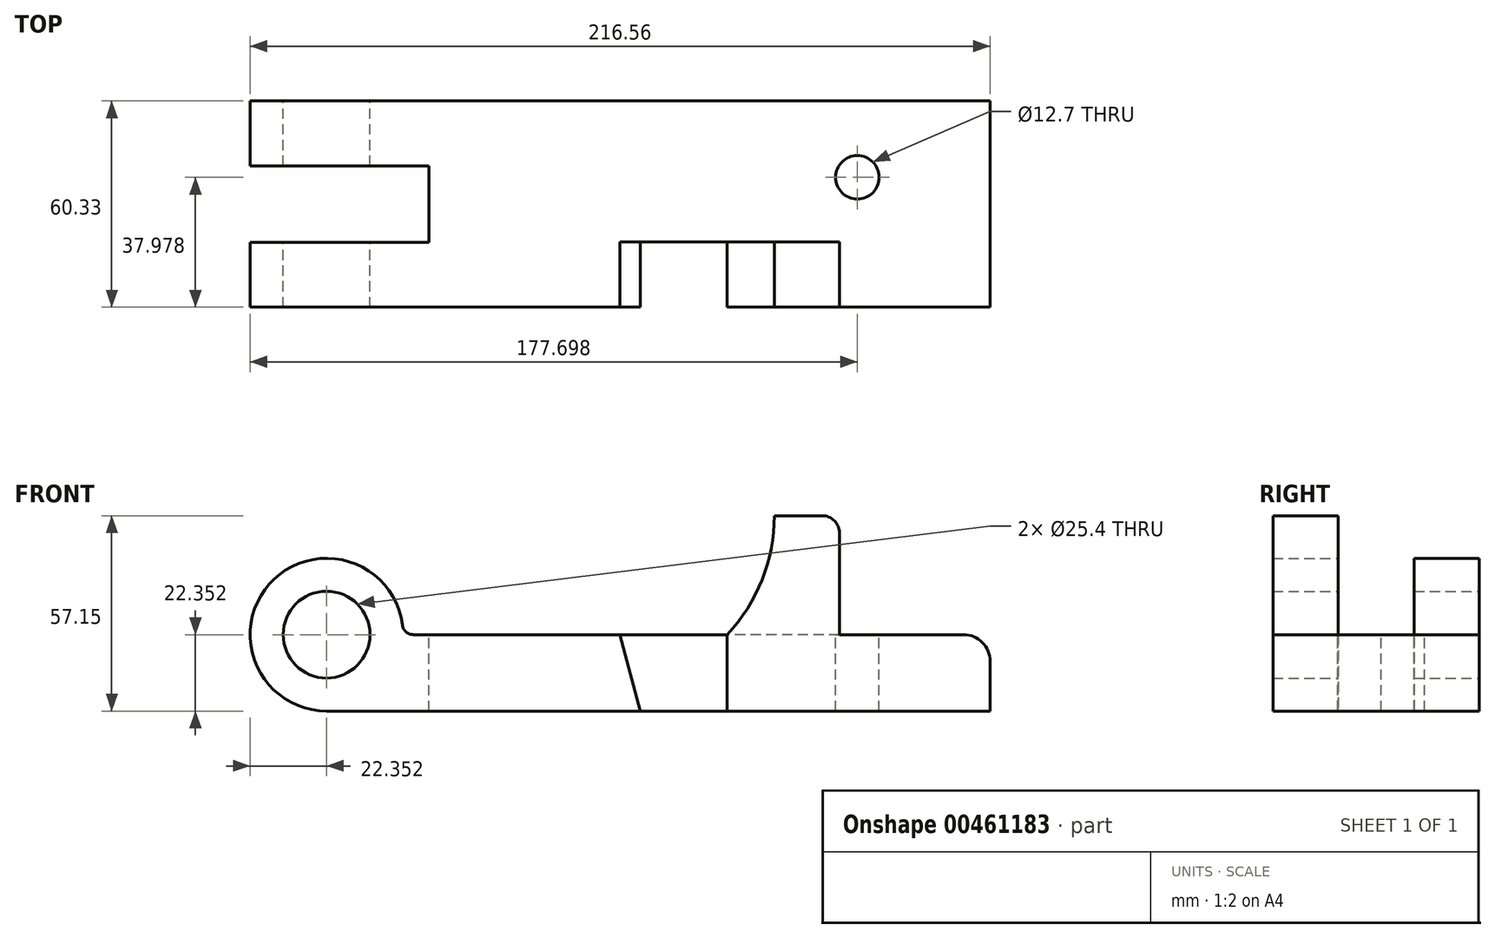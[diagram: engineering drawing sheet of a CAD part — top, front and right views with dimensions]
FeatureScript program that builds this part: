
annotation { "Feature Type Name" : "Feature", "Feature Type Description" : "" }
export const myFeature = defineFeature(function(context is Context, id is Id, definition is map)
    precondition{}
    {
        {
            var Q0;
            Q0=qCreatedBy(makeId("Front.planeOp"),FACE);
            var sketch = newSketch(context, id + "F0", { "sketchPlane" : qUnion([Q0])});
            skLineSegment(sketch, "E0", {"start": v(0, 0) * mm, "end": v(0, 14.48) * mm});
            skLineSegment(sketch, "E1", {"start": v(-7.87, 22.35) * mm, "end": v(-44.12, 22.35) * mm});
            skLineSegment(sketch, "E2", {"start": v(-44.12, 22.35) * mm, "end": v(-44.12, 52.07) * mm});
            skLineSegment(sketch, "E3", {"start": v(-49.2, 57.15) * mm, "end": v(-76.96, 57.15) * mm});
            skLineSegment(sketch, "E4", {"start": v(-76.96, 57.15) * mm, "end": v(-76.96, 22.35) * mm});
            skLineSegment(sketch, "E5", {"start": v(-76.96, 22.35) * mm, "end": v(-171.86, 22.35) * mm});
            skLineSegment(sketch, "E6", {"start": v(-194.2, 0) * mm, "end": v(0, 0) * mm});
            skArc(sketch, "E7", {"start": v(-171.86, 22.35) * mm, "mid": v(-210.01, 38.16) * mm, "end": v(-194.2, 0) * mm});
            skCircle(sketch, "E8", {"center": v(-194.2, 22.35) * mm, "radius": 12.7 * mm});
            skCircle(sketch, "E9", {"center": v(-113.97, 57.15) * mm, "radius": 50.8 * mm});
            skLineSegment(sketch, "E10", {"start": v(-76.96, 22.35) * mm, "end": v(-76.96, 0) * mm});
            skLineSegment(sketch, "E11", {"start": v(-108.36, 22.35) * mm, "end": v(-102.36, 0) * mm});
            skPoint(sketch, "E12.visualSharp", {"position": v(-44.12, 57.15) * mm});
            skArc(sketch, "E12.filletArc", {"start": v(-44.12, 52.07) * mm, "mid": v(-45.6, 55.66) * mm, "end": v(-49.2, 57.15) * mm});
            skPoint(sketch, "E13.visualSharp", {"position": v(0, 22.35) * mm});
            skArc(sketch, "E13.filletArc", {"start": v(0, 14.48) * mm, "mid": v(-2.3, 20.05) * mm, "end": v(-7.87, 22.35) * mm});
            skLineSegment(sketch, "E14", {"start": v(-44.12, 22.35) * mm, "end": v(-76.96, 22.35) * mm});
            skLineSegment(sketch, "E15", {"start": v(-194.2, 22.35) * mm, "end": v(-194.2, 9.65) * mm, "construction": true});
            skLineSegment(sketch, "E16.trimOffspring", {"start": v(-194.2, 59.62) * mm, "end": v(-194.2, 0) * mm, "construction": true});
            skSolve(sketch);
        }
        {
            var Q0;
            {var subQ0=sQuery(id+"F0.wireOp",EDGE,"E7");Q0=makeQuery(id+"F0.imprint","IMPRINT",FACE,{"disambiguationData":[TD([[makeQuery(id+"F0.imprint","IMPRINT",EDGE,{"derivedFrom":subQ0}),1.0]])]});}
            var Q1;
            {var subQ0=sQuery(id+"F0.wireOp",EDGE,"E11");var subQ1=sQuery(id+"F0.wireOp",EDGE,"E5");var subQ2=makeQuery(id+"F0.imprint","INTERSECT",VERTEX,{"derivedFrom":[subQ1,subQ0]});Q1=makeQuery(id+"F0.imprint","IMPRINT",FACE,{"disambiguationData":[TD([[makeQuery(id+"F0.imprint","IMPRINT",EDGE,{"disambiguationData":[TD([[subQ2,-1.0]])],"derivedFrom":subQ1}),1.0]])]});}
            var Q2;
            {var subQ1=sQuery(id+"F0.wireOp",EDGE,"E5");var subQ3=sQuery(id+"F0.wireOp",EDGE,"E11");var subQ4=makeQuery(id+"F0.imprint","INTERSECT",VERTEX,{"derivedFrom":[subQ1,subQ3]});Q2=makeQuery(id+"F0.imprint","IMPRINT",FACE,{"disambiguationData":[TD([[makeQuery(id+"F0.imprint","IMPRINT",EDGE,{"disambiguationData":[TD([[subQ4,-1.0]])],"derivedFrom":subQ3}),1.0]])]});}
            var Q3;
            {var subQ0=sQuery(id+"F0.wireOp",EDGE,"E10");Q3=makeQuery(id+"F0.imprint","IMPRINT",FACE,{"disambiguationData":[TD([[makeQuery(id+"F0.imprint","IMPRINT",EDGE,{"derivedFrom":subQ0}),-1.0]])]});}
            var Q4;
            {var subQ2=sQuery(id+"F0.wireOp",EDGE,"E0");Q4=makeQuery(id+"F0.imprint","IMPRINT",FACE,{"disambiguationData":[TD([[makeQuery(id+"F0.imprint","IMPRINT",EDGE,{"derivedFrom":subQ2}),1.0]])]});}
            extrude(context, id + "F1", {"entities" : qUnion([Q0, Q1, Q2, Q3, Q4]), "depth" : 60.32 * mm});
        }
        {
            var Q0;
            Q0=makeQuery(id+"F1.opExtrude","CAP_FACE",FACE,{"disambiguationData":[OSD([sQuery(id+"F0.wireOp",EDGE,"E0"),sQuery(id+"F0.wireOp",EDGE,"E1"),sQuery(id+"F0.wireOp",EDGE,"E5"),sQuery(id+"F0.wireOp",EDGE,"E6"),sQuery(id+"F0.wireOp",EDGE,"E7"),sQuery(id+"F0.wireOp",EDGE,"E8"),sQuery(id+"F0.wireOp",EDGE,"E13.filletArc"),sQuery(id+"F0.wireOp",EDGE,"E14")])],"isStart":false});
            var sketch = newSketch(context, id + "F2", { "sketchPlane" : qUnion([Q0])});
            skLineSegment(sketch, "E17.0", {"start": v(-76.96, 22.35) * mm, "end": v(-76.96, 0) * mm});
            skLineSegment(sketch, "E18.0", {"start": v(-108.36, 22.35) * mm, "end": v(-102.36, 0) * mm});
            skLineSegment(sketch, "E19.0", {"start": v(-49.2, 57.15) * mm, "end": v(-76.96, 57.15) * mm});
            skCircle(sketch, "E20.0", {"center": v(-113.97, 57.15) * mm, "radius": 50.8 * mm});
            skLineSegment(sketch, "E21.0", {"start": v(-76.96, 57.15) * mm, "end": v(-76.96, 22.35) * mm});
            skLineSegment(sketch, "E22.0", {"start": v(-76.96, 22.35) * mm, "end": v(-171.86, 22.35) * mm});
            skLineSegment(sketch, "E23.0", {"start": v(-194.2, 0) * mm, "end": v(0, 0) * mm});
            skLineSegment(sketch, "E24.0", {"start": v(-44.12, 22.35) * mm, "end": v(-44.12, 52.07) * mm});
            skArc(sketch, "E25.0", {"start": v(-44.12, 52.07) * mm, "mid": v(-45.6, 55.66) * mm, "end": v(-49.2, 57.15) * mm});
            skLineSegment(sketch, "E26.0", {"start": v(-44.12, 22.35) * mm, "end": v(-76.96, 22.35) * mm});
            skSolve(sketch);
        }
        {
            var Q0;
            Q0=makeQuery(id+"F2.imprint","IMPRINT",FACE,{"disambiguationData":[TD([[makeQuery(id+"F2.imprint","IMPRINT",EDGE,{"derivedFrom":sQuery(id+"F2.wireOp",EDGE,"E24.0")}),1.0]])]});
            extrude(context, id + "F3", {"entities" : qUnion([Q0]), "operationType" : NewBodyOperationType.ADD, "oppositeDirection" : true, "depth" : 19.05 * mm});
        }
        {
            var Q0;
            {var subQ0=sQuery(id+"F2.wireOp",EDGE,"E22.0");var subQ1=sQuery(id+"F2.wireOp",EDGE,"E18.0");var subQ2=makeQuery(id+"F2.imprint","INTERSECT",VERTEX,{"derivedFrom":[subQ1,subQ0]});Q0=makeQuery(id+"F2.imprint","IMPRINT",FACE,{"disambiguationData":[TD([[makeQuery(id+"F2.imprint","IMPRINT",EDGE,{"disambiguationData":[TD([[subQ2,-1.0]])],"derivedFrom":subQ1}),1.0]])]});}
            var Q1;
            {var subQ0=sQuery(id+"F2.wireOp",EDGE,"E17.0");Q1=makeQuery(id+"F2.imprint","IMPRINT",FACE,{"disambiguationData":[TD([[makeQuery(id+"F2.imprint","IMPRINT",EDGE,{"derivedFrom":subQ0}),-1.0]])]});}
            extrude(context, id + "F4", {"entities" : qUnion([Q0, Q1]), "operationType" : NewBodyOperationType.REMOVE, "oppositeDirection" : true, "depth" : 19.05 * mm});
        }
        {
            var Q0;
            Q0=makeQuery(id+"F1.opExtrude","SWEPT_FACE",FACE,{"disambiguationData":[OSD([sQuery(id+"F0.wireOp",EDGE,"E1"),sQuery(id+"F0.wireOp",EDGE,"E5"),sQuery(id+"F0.wireOp",EDGE,"E14")])]});
            var sketch = newSketch(context, id + "F5", { "sketchPlane" : qUnion([Q0])});
            skCircle(sketch, "E27", {"center": v(-38.86, -22.35) * mm, "radius": 6.35 * mm});
            skSolve(sketch);
        }
        {
            var Q0;
            Q0 = qSketchRegion(id + "F5", true);
            var Q1;
            Q1=makeQuery(id+"F1.opExtrude","SWEPT_FACE",FACE,{"disambiguationData":[OSD([sQuery(id+"F0.wireOp",EDGE,"E6")])]});
            extrude(context, id + "F6", {"entities" : qUnion([Q0]), "operationType" : NewBodyOperationType.REMOVE, "endBound" : BoundingType.UP_TO_SURFACE, "oppositeDirection" : true, "endBoundEntityFace" : qUnion([Q1]), "depth" : 25.4 * mm});
        }
        {
            var Q0;
            Q0=makeQuery(id+"F1.opExtrude","SWEPT_FACE",FACE,{"disambiguationData":[OSD([sQuery(id+"F0.wireOp",EDGE,"E1"),sQuery(id+"F0.wireOp",EDGE,"E5"),sQuery(id+"F0.wireOp",EDGE,"E14")])]});
            var sketch = newSketch(context, id + "F7", { "sketchPlane" : qUnion([Q0])});
            skLineSegment(sketch, "E28.bottom", {"start": v(-233.73, -19) * mm, "end": v(-164.24, -19) * mm});
            skLineSegment(sketch, "E28.top", {"start": v(-233.73, -41.33) * mm, "end": v(-164.24, -41.33) * mm});
            skLineSegment(sketch, "E28.left", {"start": v(-233.73, -19) * mm, "end": v(-233.73, -41.33) * mm});
            skLineSegment(sketch, "E28.right", {"start": v(-164.24, -19) * mm, "end": v(-164.24, -41.33) * mm});
            skSolve(sketch);
        }
        {
            var Q0;
            Q0=makeQuery(id+"F1.opExtrude","SWEPT_EDGE",EDGE,{"disambiguationData":[OSD([sQuery(id+"F0.wireOp",EDGE,"E5"),sQuery(id+"F0.wireOp",EDGE,"E7")])]});
            var Q1;
            Q1=makeQuery(id+"F3.opExtrude","SWEPT_EDGE",EDGE,{"disambiguationData":[OSD([sQuery(id+"F0.wireOp",EDGE,"E1"),sQuery(id+"F0.wireOp",EDGE,"E5"),sQuery(id+"F0.wireOp",EDGE,"E14"),sQuery(id+"F2.wireOp",EDGE,"E24.0"),sQuery(id+"F2.wireOp",EDGE,"E26.0")])]});
            fillet(context, id + "F8", {"entities" : qUnion([Q0, Q1]), "radius" : 3.3 * mm, "tangentPropagation" : true, "allowEdgeOverflow" : false});
        }
        {
            var Q0;
            Q0 = qSketchRegion(id + "F7", true);
            extrude(context, id + "F9", {"entities" : qUnion([Q0]), "operationType" : NewBodyOperationType.REMOVE, "endBound" : BoundingType.SYMMETRIC, "oppositeDirection" : true, "depth" : 127 * mm});
        }
    });
